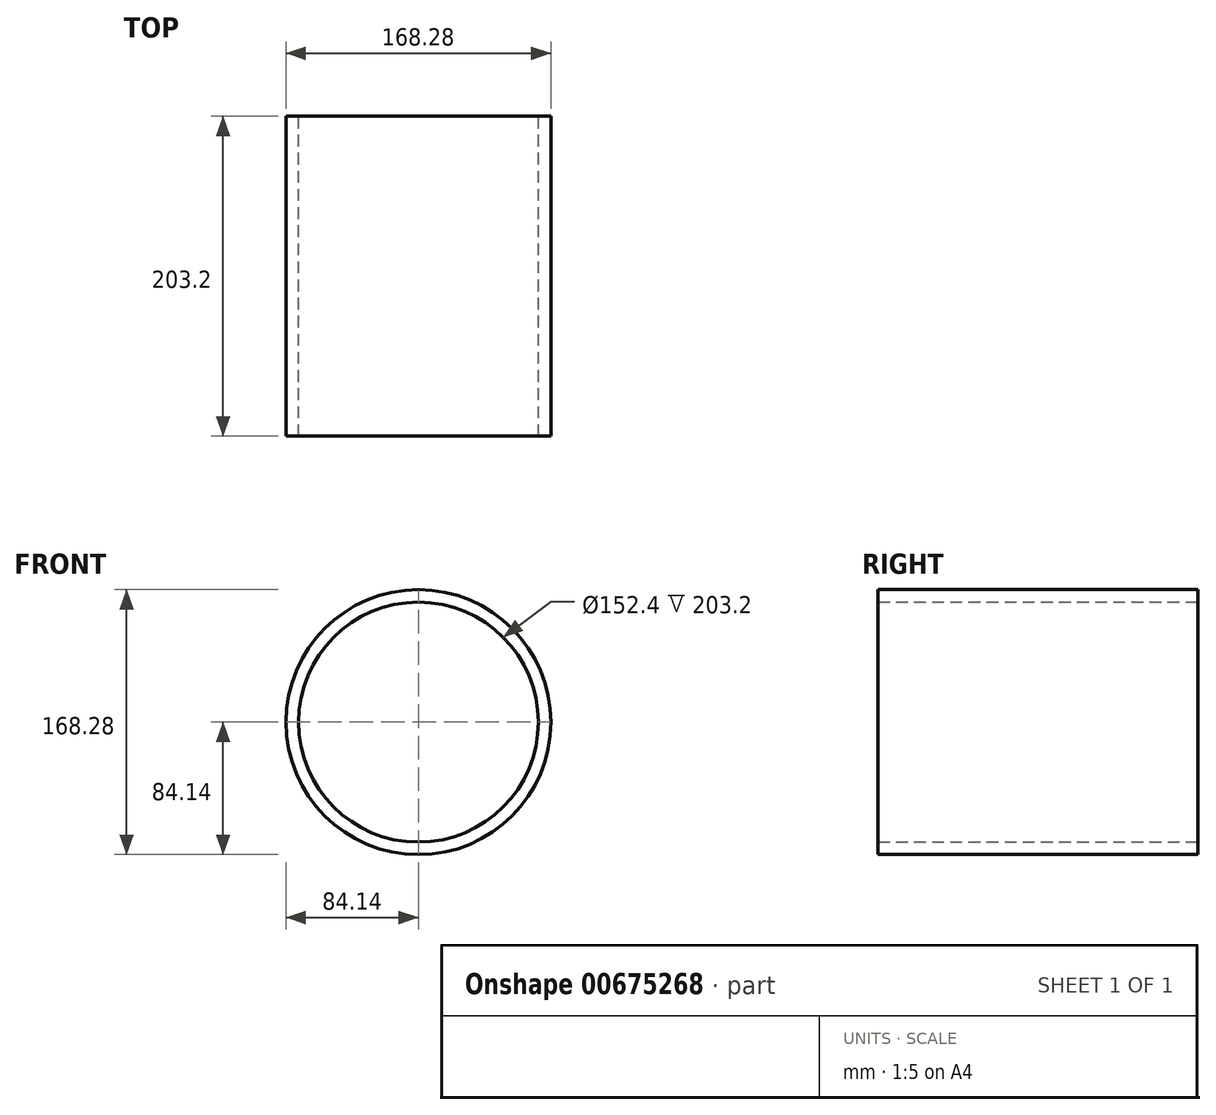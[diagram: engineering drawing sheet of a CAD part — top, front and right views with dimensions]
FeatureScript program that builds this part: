
annotation { "Feature Type Name" : "Feature", "Feature Type Description" : "" }
export const myFeature = defineFeature(function(context is Context, id is Id, definition is map)
    precondition{}
    {
        {
            var Q0;
            Q0=qCreatedBy(makeId("Front.planeOp"),FACE);
            var sketch = newSketch(context, id + "F0", { "sketchPlane" : qUnion([Q0])});
            skCircle(sketch, "E0", {"center": v(0, 0) * mm, "radius": 76.2 * mm});
            skCircle(sketch, "E1", {"center": v(0, 0) * mm, "radius": 84.14 * mm});
            skSolve(sketch);
        }
        {
            var Q0;
            Q0 = qSketchRegion(id + "F0", true);
            extrude(context, id + "F1", {"entities" : qUnion([Q0]), "depth" : 203.2 * mm, "offsetDistance" : 25.4 * mm});
        }
    });
